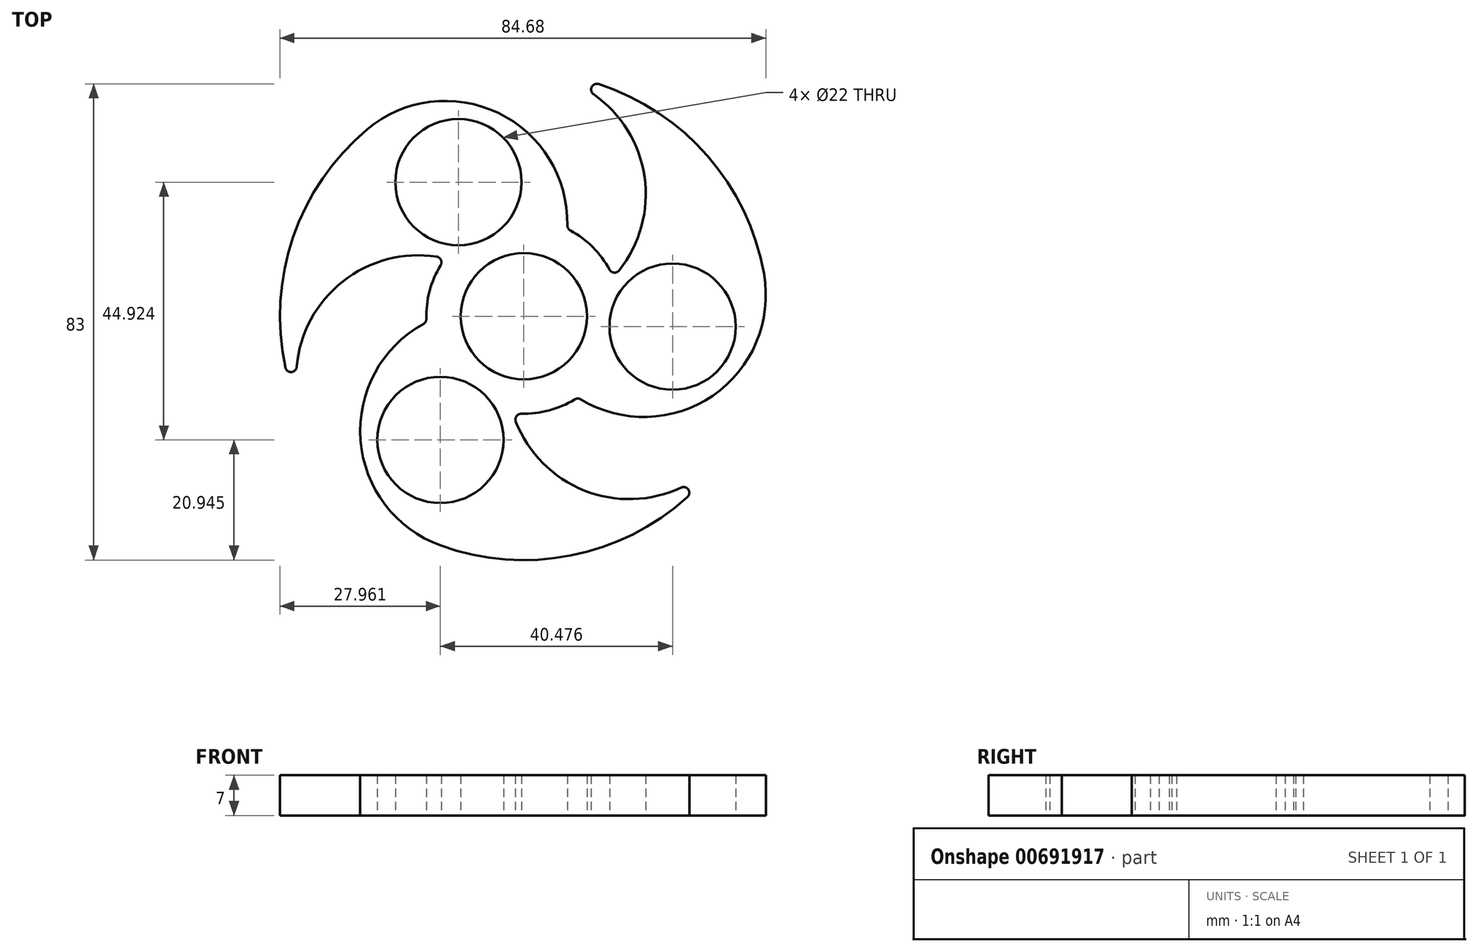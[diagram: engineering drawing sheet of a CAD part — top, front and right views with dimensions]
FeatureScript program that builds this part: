
annotation { "Feature Type Name" : "Feature", "Feature Type Description" : "" }
export const myFeature = defineFeature(function(context is Context, id is Id, definition is map)
    precondition{}
    {
        {
            var Q0;
            Q0=qCreatedBy(makeId("Top.planeOp"),FACE);
            var sketch = newSketch(context, id + "F0", { "sketchPlane" : qUnion([Q0])});
            skArc(sketch, "E0", {"start": v(41.85, 7.38) * mm, "mid": v(32.04, 27.92) * mm, "end": v(13.03, 40.45) * mm});
            skLineSegment(sketch, "E1", {"start": v(0, 0) * mm, "end": v(0, 11) * mm});
            skArc(sketch, "E2", {"start": v(-10.63, 2.85) * mm, "mid": v(0, 0) * mm, "end": v(10.63, 2.85) * mm});
            skArc(sketch, "E3.1.0", {"start": v(2.85, -10.63) * mm, "mid": v(0, 0) * mm, "end": v(-7.78, 7.78) * mm});
            skArc(sketch, "E3.2.0", {"start": v(7.78, 7.78) * mm, "mid": v(0, 0) * mm, "end": v(-2.85, -10.63) * mm});
            skCircle(sketch, "E4", {"center": v(0, 0) * mm, "radius": 11 * mm});
            skArc(sketch, "E5", {"start": v(-14.5, 8.87) * mm, "mid": v(-16.42, 4.4) * mm, "end": v(-17, -0.45) * mm});
            skLineSegment(sketch, "E6", {"start": v(0, 0) * mm, "end": v(10.83, 1.91) * mm});
            skArc(sketch, "E7", {"start": v(0.96, 10.96) * mm, "mid": v(0, 0) * mm, "end": v(4.65, -9.97) * mm});
            skArc(sketch, "E8.1.0", {"start": v(-9.97, -4.65) * mm, "mid": v(0, 0) * mm, "end": v(6.3, 9.01) * mm});
            skArc(sketch, "E8.2.0", {"start": v(9.01, -6.3) * mm, "mid": v(0, 0) * mm, "end": v(-10.96, 0.96) * mm});
            skPoint(sketch, "E9.orphan", {"position": v(41.85, 7.38) * mm});
            skArc(sketch, "E10.trimOffspring", {"start": v(-14.54, -39.94) * mm, "mid": v(8.16, -41.7) * mm, "end": v(28.51, -31.51) * mm});
            skArc(sketch, "E11.trimOffspring", {"start": v(-27.32, 32.56) * mm, "mid": v(-40.2, 13.79) * mm, "end": v(-41.55, -8.94) * mm});
            skArc(sketch, "E12.trimOffspring", {"start": v(7.59, 15.84) * mm, "mid": v(-4.48, 35.44) * mm, "end": v(-27.32, 32.56) * mm});
            skArc(sketch, "E13.trimOffspring", {"start": v(16.6, 7.98) * mm, "mid": v(21.03, 24.29) * mm, "end": v(12.16, 38.68) * mm});
            skArc(sketch, "E14.trimOffspring", {"start": v(9.93, -14.5) * mm, "mid": v(32.94, -13.84) * mm, "end": v(41.85, 7.38) * mm});
            skArc(sketch, "E15.trimOffspring", {"start": v(-1.39, -18.36) * mm, "mid": v(10.52, -30.36) * mm, "end": v(27.42, -29.87) * mm});
            skArc(sketch, "E16.trimOffspring", {"start": v(-17.51, -1.35) * mm, "mid": v(-28.46, -21.6) * mm, "end": v(-14.54, -39.94) * mm});
            skArc(sketch, "E17.trimOffspring", {"start": v(-15.2, 10.38) * mm, "mid": v(-31.55, 6.07) * mm, "end": v(-39.58, -8.81) * mm});
            skArc(sketch, "E18.trimOffspring", {"start": v(-0.43, -17) * mm, "mid": v(4.4, -16.42) * mm, "end": v(8.89, -14.5) * mm});
            skArc(sketch, "E19.trimOffspring", {"start": v(14.93, 8.12) * mm, "mid": v(12.02, 12.03) * mm, "end": v(8.1, 14.94) * mm});
            skLineSegment(sketch, "E20", {"start": v(0, 0) * mm, "end": v(-21.92, 44.94) * mm});
            skCircle(sketch, "E21", {"center": v(-11.4, 23.37) * mm, "radius": 11 * mm});
            skCircle(sketch, "E22.1.0", {"center": v(-14.54, -21.55) * mm, "radius": 11 * mm});
            skCircle(sketch, "E22.2.0", {"center": v(25.94, -1.81) * mm, "radius": 11 * mm});
            skPoint(sketch, "E23.visualSharp", {"position": v(-36.8, -21.25) * mm});
            skArc(sketch, "E23.filletArc", {"start": v(-41.55, -8.94) * mm, "mid": v(-40.5, -9.73) * mm, "end": v(-39.58, -8.81) * mm});
            skPoint(sketch, "E24.visualSharp", {"position": v(0, 42.5) * mm});
            skArc(sketch, "E24.filletArc", {"start": v(13.03, 40.45) * mm, "mid": v(11.83, 39.94) * mm, "end": v(12.16, 38.68) * mm});
            skPoint(sketch, "E25.visualSharp", {"position": v(36.8, -21.25) * mm});
            skArc(sketch, "E25.filletArc", {"start": v(28.51, -31.51) * mm, "mid": v(28.68, -30.22) * mm, "end": v(27.42, -29.87) * mm});
            skPoint(sketch, "E26.visualSharp", {"position": v(-1.9, -16.9) * mm});
            skArc(sketch, "E26.filletArc", {"start": v(-0.43, -17) * mm, "mid": v(-1.28, -17.42) * mm, "end": v(-1.39, -18.36) * mm});
            skPoint(sketch, "E27.visualSharp", {"position": v(9.4, -14.16) * mm});
            skArc(sketch, "E27.filletArc", {"start": v(9.93, -14.5) * mm, "mid": v(9.4, -14.35) * mm, "end": v(8.89, -14.5) * mm});
            skPoint(sketch, "E28.visualSharp", {"position": v(15.58, 6.8) * mm});
            skArc(sketch, "E28.filletArc", {"start": v(14.93, 8.12) * mm, "mid": v(15.72, 7.6) * mm, "end": v(16.6, 7.98) * mm});
            skPoint(sketch, "E29.visualSharp", {"position": v(7.56, 15.22) * mm});
            skArc(sketch, "E29.filletArc", {"start": v(7.59, 15.84) * mm, "mid": v(7.72, 15.32) * mm, "end": v(8.1, 14.94) * mm});
            skPoint(sketch, "E30.visualSharp", {"position": v(-13.68, 10.1) * mm});
            skArc(sketch, "E30.filletArc", {"start": v(-14.5, 8.87) * mm, "mid": v(-14.45, 9.82) * mm, "end": v(-15.2, 10.38) * mm});
            skPoint(sketch, "E31.visualSharp", {"position": v(-16.97, -1.06) * mm});
            skArc(sketch, "E31.filletArc", {"start": v(-17.51, -1.35) * mm, "mid": v(-17.13, -0.97) * mm, "end": v(-17, -0.45) * mm});
            skSolve(sketch);
        }
        {
            var Q0;
            Q0 = qSketchRegion(id + "F0", true);
            extrude(context, id + "F1", {"entities" : qUnion([Q0]), "depth" : 7 * mm, "offsetDistance" : 25 * mm});
        }
    });
